# Revit family: Legrand_Practibox³_8_y_12_módulos_puerta_blanca
name_source: partatom
category: Equipement électrique
revit_build: Autodesk Revit 2018 (Build: 20170223_1515(x64)
units: mm (PartAtom-declared; Revit-internal decimal feet)

## family parameters
Basée sur le plan de construction = Non
Configuration du panneau = Deux colonnes, circuits au sein
Cote de connecteur circulaire = Utiliser le diamètre
Couper avec des vides une fois chargée = Non
Numéro OmniClass = 23.80.30.11.17
Partagée = Non
Point de calcul de pièce = Non
Titre OmniClass = Distribution Boards and Control Panels
Toujours verticalement = Oui
Type d'élément = Tableau de raccordement

## types (8) — shared parameters
Condiciones Generales de Uso = https://export.legrand.com
Fabricant = Legrand
Modèle = Practibox³
URL = www.legrand.com
puerta blanca = Oui
puerta transparente = Non

## per-type parameters (varying)
| type | 401711 | 401712 | 401713 | 401714 | 401761 | 401762 | 401763 | 401764 | Altura | Bornas N | Bornas T | anchura | profundidad |
| Practibox³ 1x8 módulos 401711 | Oui | Non | Non | Non | Non | Non | Non | Non | 208 mm  [stored 0.682415 ft] |  | terminal 8 hoyos | 286 mm | 100 mm  [stored 0.328084 ft] |
| Practibox³ 1x12 módulos 401712 | Non | Oui | Non | Non | Non | Non | Non | Non | 246 mm  [stored 0.807087 ft] |  | terminal 13 hoyos | 359 mm  [stored 1.17782 ft] | 100 mm  [stored 0.328084 ft] |
| Practibox³ 2+12 módulos 401713 | Non | Non | Oui | Non | Non | Non | Non | Non | 396 mm  [stored 1.29921 ft] |  | terminal 17 hoyos | 359 mm  [stored 1.17782 ft] | 105 mm  [stored 0.344488 ft] |
| Practibox³ 3x12 módulos 401714 | Non | Non | Non | Oui | Non | Non | Non | Non | 546 mm  [stored 1.79134 ft] |  | terminal 22 hoyos | 359 mm  [stored 1.17782 ft] | 105 mm  [stored 0.344488 ft] |
| Practibox³ 1x8 módulos 401761 | Non | Non | Non | Non | Oui | Non | Non | Non | 208 mm  [stored 0.682415 ft] | terminal 8 hoyos | terminal 8 hoyos | 286 mm | 100 mm  [stored 0.328084 ft] |
| Practibox³ 1x12 módulos 401762 | Non | Non | Non | Non | Non | Oui | Non | Non | 246 mm  [stored 0.807087 ft] | terminal 8 hoyos | terminal 13 hoyos | 359 mm  [stored 1.17782 ft] | 100 mm  [stored 0.328084 ft] |
| Practibox³ 2+12 módulos 401763 | Non | Non | Non | Non | Non | Non | Oui | Non | 396 mm  [stored 1.29921 ft] | terminal 2x8 hoyos | terminal 17 hoyos | 359 mm  [stored 1.17782 ft] | 105 mm  [stored 0.344488 ft] |
| Practibox³ 3x12 módulos 401764 | Non | Non | Non | Non | Non | Non | Non | Oui | 546 mm  [stored 1.79134 ft] | terminal 3x8 hoyos | terminal 22 hoyos | 359 mm  [stored 1.17782 ft] | 105 mm  [stored 0.344488 ft] |

note: [stored X ft] marks values corroborated as IEEE doubles in the binary element streams (Revit-internal decimal feet)
